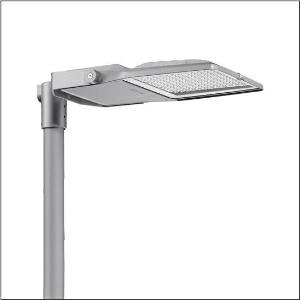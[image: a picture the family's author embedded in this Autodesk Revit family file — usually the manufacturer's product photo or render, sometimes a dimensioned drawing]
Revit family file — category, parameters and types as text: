
# Revit family: floodlight_fl_21_midi___pl43_5xa7785f2a3a_ea2c
name_source: partatom
category: Lighting Fixtures
units: mm (PartAtom-declared; Revit-internal decimal feet)

## family parameters
Cut with Voids When Loaded = No
Host = Face
Light Source = No
Part Type = Normal
Room Calculation Point = No
Round Connector Dimension = Use Diameter
Shared = No

## types (1)
- --- (1 x LED, 36680 lm, 271.6 W, 3000K)
    Apparent Load = 272 VA
    CIE Flux Codes = 27 78 99 100 100
    Color Rendering = 70
    Color Temperature = 3000K
    Default Elevation = 1800 mm
    Description = Floodlight FL 21 midi, floodlight, primary light control with lens, of PMMA, primary optical cover: protective disc, of toughened safety glass, transparent, light distribution: PL43, light emission: direct distribution, installation type: surface-mounted, LED, High Power LED, rated luminous flux: 36.680lm, luminous efficacy: 135lm/W, light colour: 730, colour temperature: 3000K, control gear: ECG Smart Interface, control: flexible luminous flux parameterisation, time-dependent luminous flux control, constant luminous flux control, overheat protection, presetting dimming logarithmic, with terminal, 6-pole, mains connection: 220..240V, AC, 50/60Hz, start of lifetime: 272W, end of service life: 287W, reduction: 123W, luminaire housing, of diecast aluminium, powder-coated, Siteco® metallic grey (DB 702S), sealing non-destructively replaceable, please order mast flange separately, mast bracket, of steel, galvanised, powder-coated, Siteco® metallic grey (DB 702S), Smart Interface above, protection rating (complete): IP66, insulation class (complete): insulation class II (safety insulation), certification: CE, protection symbol: D, impact resistance: IK08, permissible operating ambient temperature: -40..+40°C, permissible operating ambient temperature for outdoor applications: -40..+50°C, standard: DIN EN 12944, LABS conformity tested according to VDMA 24364:2018-05, packaging unit: 1 piece

Light Distribution: PL43
    Height = 76 mm
    Lamp = 1 x LED
    Lamp Light Flux = 36680 lm
    Lamp Power = 271.6 W
    Lamp count = 1
    Length = 657 mm
    Luminous efficacy = 135 lm/W
    Manufacturer = Siteco
    ModVariant = No
    Model = 5XA7785F2A3A
    Number of Poles = 1
    OnlyDefault = Yes
    Power Factor = 1
    Product Name = Floodlight FL 21 midi | PL43
    Product group = floodlight | pylon annexe
    ProductGroupID = 6200
    Protection Class = Protection class II
    Protection Degree = IP 66
    RLX_Detail_Level = 1
    RLX_Emergency_Light_Flux = 0 lm
    RLX_Emergency_Type = 0
    RLX_Emergency_Type_DB = No
    RlxData = <blob elided: 153197 chars, md5=9c03de11>
    Socket = socket
    Standby Power = 0 W
    System Light Flux = 36680 lm
    System Power = 272 W
    Type Comments = factory setting: luminous flux: 100 % | dim-lin: 254 | 620 mA
    Type Image = l_1007123.jpg
    URL = http://relux.com
    VarID = @adj_128359
    Voltage = 0 V
    Weight = 0.00 kg
    Width = 442 mm

## geometry (parser evidence)
native form markers: Blend x4, Sweep x11
no freeform markers — native parametric forms only
